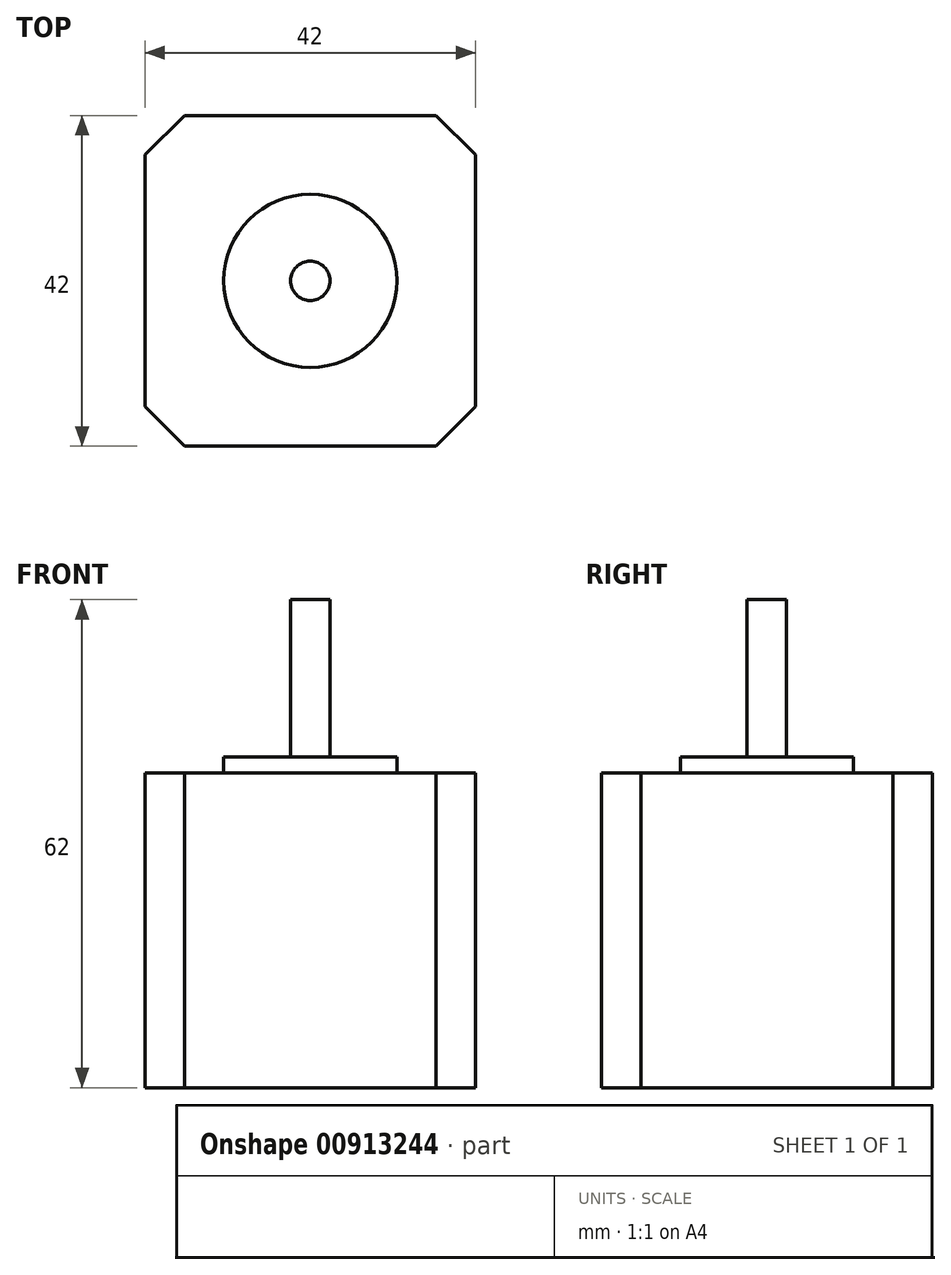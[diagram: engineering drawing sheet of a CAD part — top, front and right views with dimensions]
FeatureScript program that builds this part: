
annotation { "Feature Type Name" : "Feature", "Feature Type Description" : "" }
export const myFeature = defineFeature(function(context is Context, id is Id, definition is map)
    precondition{}
    {
        {
            var Q0;
            Q0=qCreatedBy(makeId("Top.planeOp"),FACE);
            var sketch = newSketch(context, id + "F0", { "sketchPlane" : qUnion([Q0])});
            skLineSegment(sketch, "E0.bottom", {"start": v(21, -21) * mm, "end": v(-21, -21) * mm});
            skLineSegment(sketch, "E0.top", {"start": v(21, 21) * mm, "end": v(-21, 21) * mm});
            skLineSegment(sketch, "E0.left", {"start": v(21, -21) * mm, "end": v(21, 21) * mm});
            skLineSegment(sketch, "E0.right", {"start": v(-21, -21) * mm, "end": v(-21, 21) * mm});
            skPoint(sketch, "E0.middle", {"position": v(0, 0) * mm});
            skSolve(sketch);
        }
        {
            var Q0;
            Q0=makeQuery(id+"F0.imprint","IMPRINT",FACE,{"disambiguationData":[TD([[makeQuery(id+"F0.imprint","IMPRINT",EDGE,{"derivedFrom":sQuery(id+"F0.wireOp",EDGE,"E0.bottom")}),-1.0]])]});
            extrude(context, id + "F1", {"entities" : qUnion([Q0]), "flatOperationType" : FlatOperationType.REMOVE, "depth" : 40 * mm, "offsetDistance" : 25 * mm, "domain" : OperationDomain.MODEL});
        }
        {
            var Q0;
            Q0=makeQuery(id+"F1.opExtrude","CAP_FACE",FACE,{"disambiguationData":[OSD([sQuery(id+"F0.wireOp",EDGE,"E0.bottom"),sQuery(id+"F0.wireOp",EDGE,"E0.top"),sQuery(id+"F0.wireOp",EDGE,"E0.left"),sQuery(id+"F0.wireOp",EDGE,"E0.right")])],"isStart":false});
            var sketch = newSketch(context, id + "F2", { "sketchPlane" : qUnion([Q0])});
            skCircle(sketch, "E1", {"center": v(0, 0) * mm, "radius": 11 * mm});
            skSolve(sketch);
        }
        {
            var Q0;
            Q0=makeQuery(id+"F2.imprint","IMPRINT",FACE,{"disambiguationData":[TD([[makeQuery(id+"F2.imprint","IMPRINT",EDGE,{"derivedFrom":sQuery(id+"F2.wireOp",EDGE,"E1")}),1.0]])]});
            extrude(context, id + "F3", {"entities" : qUnion([Q0]), "operationType" : NewBodyOperationType.ADD, "flatOperationType" : FlatOperationType.REMOVE, "depth" : 2 * mm, "offsetDistance" : 25 * mm, "domain" : OperationDomain.MODEL});
        }
        {
            var Q0;
            Q0=makeQuery(id+"F3.opExtrude","CAP_FACE",FACE,{"disambiguationData":[OSD([sQuery(id+"F2.wireOp",EDGE,"E1")])],"isStart":false});
            var sketch = newSketch(context, id + "F4", { "sketchPlane" : qUnion([Q0])});
            skCircle(sketch, "E2", {"center": v(0, 0) * mm, "radius": 2.5 * mm});
            skSolve(sketch);
        }
        {
            var Q0;
            Q0=makeQuery(id+"F4.imprint","IMPRINT",FACE,{"disambiguationData":[TD([[makeQuery(id+"F4.imprint","IMPRINT",EDGE,{"derivedFrom":sQuery(id+"F4.wireOp",EDGE,"E2")}),1.0]])]});
            extrude(context, id + "F5", {"entities" : qUnion([Q0]), "operationType" : NewBodyOperationType.ADD, "flatOperationType" : FlatOperationType.REMOVE, "depth" : 20 * mm, "offsetDistance" : 25 * mm, "domain" : OperationDomain.MODEL});
        }
        {
            var Q0;
            Q0=makeQuery(id+"F1.opExtrude","SWEPT_EDGE",EDGE,{"disambiguationData":[OSD([sQuery(id+"F0.wireOp",EDGE,"E0.bottom"),sQuery(id+"F0.wireOp",EDGE,"E0.left")])]});
            var Q1;
            Q1=makeQuery(id+"F1.opExtrude","SWEPT_EDGE",EDGE,{"disambiguationData":[OSD([sQuery(id+"F0.wireOp",EDGE,"E0.top"),sQuery(id+"F0.wireOp",EDGE,"E0.right")])]});
            var Q2;
            Q2=makeQuery(id+"F1.opExtrude","SWEPT_EDGE",EDGE,{"disambiguationData":[OSD([sQuery(id+"F0.wireOp",EDGE,"E0.bottom"),sQuery(id+"F0.wireOp",EDGE,"E0.right")])]});
            var Q3;
            Q3=makeQuery(id+"F1.opExtrude","SWEPT_EDGE",EDGE,{"disambiguationData":[OSD([sQuery(id+"F0.wireOp",EDGE,"E0.top"),sQuery(id+"F0.wireOp",EDGE,"E0.left")])]});
            chamfer(context, id + "F6", {"entities" : qUnion([Q0, Q1, Q2, Q3]), "width" : 5 * mm, "tangentPropagation" : true});
        }
    });
